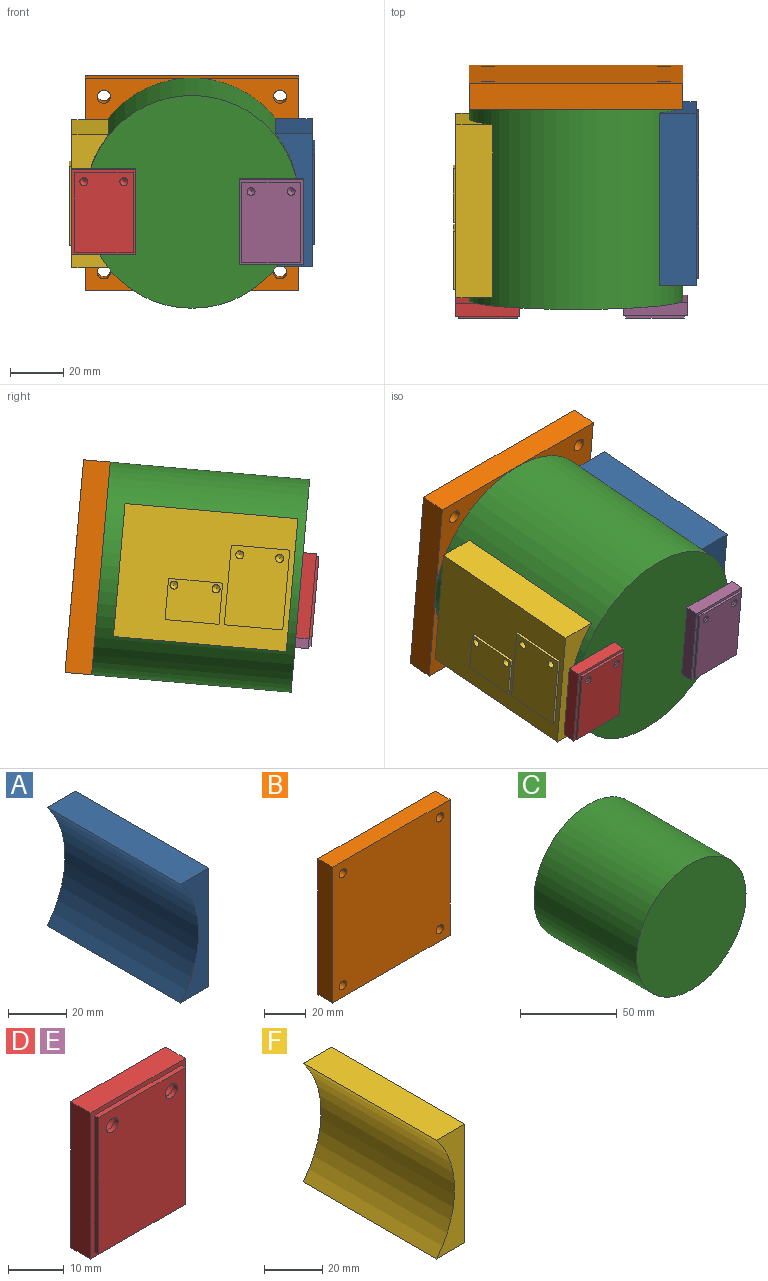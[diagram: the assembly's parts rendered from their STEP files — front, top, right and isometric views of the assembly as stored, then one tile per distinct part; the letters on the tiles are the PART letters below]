
ASSEMBLY  parts=6 mates=5
PART A: 35 faces, bbox 14.8x65x50 mm
  f0: plane 65x50mm, normal (1,0,0), area 1512mm2, adj f2,f3,f4,f5,f6,f7,f8,f9
  f1: cylinder r=40mm len=65mm, axis (0,1,0), area 3510.7mm2, adj f2,f3,f4,f5
  f2: plane 65x13.78mm, normal (0,0,-1), area 895.4mm2, adj f0,f1,f4,f5
  f3: plane 65x13.78mm, normal (0,0,1), area 895.4mm2, adj f0,f1,f4,f5
  f4: plane 50x13.78mm, normal (0,-1,0), area 389.2mm2, adj f0,f1,f2,f3
  f5: plane 50x13.78mm, normal (0,1,0), area 389.2mm2, adj f0,f1,f2,f3
  f6: plane 19x1mm, normal (0,0,1), area 19mm2, adj f0,f7,f9,f10
  f7: plane 34x1mm, normal (0,-1,0), area 34mm2, adj f0,f6,f8,f10
  f8: plane 19x1mm, normal (0,0,-1), area 19mm2, adj f0,f7,f9,f10
  f9: plane 34x1mm, normal (0,1,0), area 34mm2, adj f0,f6,f8,f10
  f10: plane 34x19mm, normal (1,0,0), area 636.2mm2, adj f6,f7,f8,f9,f26,f28
  f11: plane 16x1mm, normal (0,0,1), area 16mm2, adj f0,f12,f14,f15
  f12: plane 27x1mm, normal (0,-1,0), area 27mm2, adj f0,f11,f13,f15
  f13: plane 16x1mm, normal (0,0,-1), area 16mm2, adj f0,f12,f14,f15
  f14: plane 27x1mm, normal (0,1,0), area 27mm2, adj f0,f11,f13,f15
  f15: plane 27x16mm, normal (1,0,0), area 422.2mm2, adj f11,f12,f13,f14,f22,f24
  f16: plane 22x1mm, normal (0,0,1), area 22mm2, adj f0,f17,f19,f20
  f17: plane 30x1mm, normal (0,-1,0), area 30mm2, adj f0,f16,f18,f20
  f18: plane 22x1mm, normal (0,0,-1), area 22mm2, adj f0,f17,f19,f20
  f19: plane 30x1mm, normal (0,1,0), area 30mm2, adj f0,f16,f18,f20
  f20: plane 30x22mm, normal (1,0,0), area 626.2mm2, adj f16,f17,f18,f19,f30,f32,f34
  f21: cone r=0mm half-angle=59deg, axis (1,0,0), area 5.7mm2, adj f22
  f22: cylinder r=1.25mm len=5mm, axis (1,0,0), area 39.3mm2, adj f15,f21
  f23: cone r=0mm half-angle=59deg, axis (1,0,0), area 5.7mm2, adj f24
  f24: cylinder r=1.25mm len=5mm, axis (1,0,0), area 39.3mm2, adj f15,f23
  f25: cone r=0mm half-angle=59deg, axis (1,0,0), area 5.7mm2, adj f26
  f26: cylinder r=1.25mm len=5mm, axis (1,0,0), area 39.3mm2, adj f10,f25
  f27: cone r=0mm half-angle=59deg, axis (1,0,0), area 5.7mm2, adj f28
  f28: cylinder r=1.25mm len=5mm, axis (1,0,0), area 39.3mm2, adj f10,f27
  f29: cone r=0mm half-angle=59deg, axis (1,0,0), area 8.2mm2, adj f30
  f30: cylinder r=1.5mm len=5mm, axis (1,0,0), area 47.1mm2, adj f20,f29
  f31: cone r=0mm half-angle=59deg, axis (1,0,0), area 8.2mm2, adj f32
  f32: cylinder r=1.5mm len=5mm, axis (1,0,0), area 47.1mm2, adj f20,f31
  f33: cone r=0mm half-angle=59deg, axis (1,0,0), area 22.9mm2, adj f34
  f34: cylinder r=2.5mm len=5mm, axis (1,0,0), area 78.5mm2, adj f20,f33
PART B: 10 faces, bbox 80x10x80 mm
  f0: plane 80x10mm, normal (1,0,0), area 800mm2, adj f1,f6,f8,f9
  f1: plane 80x10mm, normal (0,0,1), area 800mm2, adj f0,f2,f8,f9
  f2: plane 80x10mm, normal (-1,0,0), area 800mm2, adj f1,f6,f8,f9
  f3: cylinder r=2.5mm len=10mm, axis (0,1,0), area 157.1mm2, adj f8,f9
  f4: cylinder r=2.5mm len=10mm, axis (0,1,0), area 157.1mm2, adj f8,f9
  f5: cylinder r=2.5mm len=10mm, axis (0,1,0), area 157.1mm2, adj f8,f9
  f6: plane 80x10mm, normal (0,0,-1), area 800mm2, adj f0,f2,f8,f9
  f7: cylinder r=2.5mm len=10mm, axis (0,1,0), area 157.1mm2, adj f8,f9
  f8: plane 80x80mm, normal (0,-1,0), area 6321.5mm2, adj f0,f1,f2,f3,f4,f5,f6,f7
  f9: plane 80x80mm, normal (0,1,0), area 6321.5mm2, adj f0,f1,f2,f3,f4,f5,f6,f7
PART C: 3 faces, bbox 80x75x80 mm
  f0: cylinder r=40mm len=80mm, axis (0,1,0), area 18849.6mm2, adj f1,f2
  f1: plane 80x80mm, normal (0,-1,0), area 5026.5mm2, adj f0
  f2: plane 80x80mm, normal (0,1,0), area 5026.5mm2, adj f0
PART D: 15 faces, bbox 24x6x32 mm
  f0: plane 22x1mm, normal (0,0,1), area 22mm2, adj f1,f3,f4,f9
  f1: plane 30x1mm, normal (-1,0,0), area 30mm2, adj f0,f2,f4,f9
  f2: plane 22x1mm, normal (0,0,-1), area 22mm2, adj f1,f3,f4,f9
  f3: plane 30x1mm, normal (1,0,0), area 30mm2, adj f0,f2,f4,f9
  f4: plane 30x22mm, normal (0,-1,0), area 645.9mm2, adj f0,f1,f2,f3,f12,f14
  f5: plane 32x5mm, normal (1,0,0), area 160mm2, adj f6,f8,f9,f10
  f6: plane 24x5mm, normal (0,0,1), area 120mm2, adj f5,f7,f9,f10
  f7: plane 32x5mm, normal (-1,0,0), area 160mm2, adj f6,f8,f9,f10
  f8: plane 24x5mm, normal (0,0,-1), area 120mm2, adj f5,f7,f9,f10
  f9: plane 32x24mm, normal (0,-1,0), area 108mm2, adj f0,f1,f2,f3,f5,f6,f7,f8
  f10: plane 32x24mm, normal (0,1,0), area 768mm2, adj f5,f6,f7,f8
  f11: cone r=0mm half-angle=59deg, axis (0,-1,0), area 8.2mm2, adj f12
  f12: cylinder r=1.5mm len=3mm, axis (0,-1,0), area 9.4mm2, adj f4,f11
  f13: cone r=0mm half-angle=59deg, axis (0,-1,0), area 8.2mm2, adj f14
  f14: cylinder r=1.5mm len=3mm, axis (0,-1,0), area 9.4mm2, adj f4,f13
PART E: same geometry as D
PART F: 24 faces, bbox 14.8x65x50 mm
  f0: plane 65x50mm, normal (1,0,0), area 2275.3mm2, adj f2,f3,f4,f5,f6,f7,f8,f9
  f1: cylinder r=40mm len=65mm, axis (0,1,0), area 3510.7mm2, adj f2,f3,f4,f5
  f2: plane 65x13.78mm, normal (0,0,-1), area 895.4mm2, adj f0,f1,f4,f5
  f3: plane 65x13.78mm, normal (0,0,1), area 895.4mm2, adj f0,f1,f4,f5
  f4: plane 50x13.78mm, normal (0,-1,0), area 389.2mm2, adj f0,f1,f2,f3
  f5: plane 50x13.78mm, normal (0,1,0), area 389.2mm2, adj f0,f1,f2,f3
  f6: plane 22x1mm, normal (0,0,1), area 22mm2, adj f0,f7,f9,f10
  f7: plane 30x1mm, normal (0,-1,0), area 30mm2, adj f0,f6,f8,f10
  f8: plane 22x1mm, normal (0,0,-1), area 22mm2, adj f0,f7,f9,f10
  f9: plane 30x1mm, normal (0,1,0), area 30mm2, adj f0,f6,f8,f10
  f10: plane 30x22mm, normal (1,0,0), area 645.9mm2, adj f6,f7,f8,f9,f21,f23
  f11: plane 15.5x1mm, normal (0,-1,0), area 15.5mm2, adj f0,f12,f14,f15
  f12: plane 20.3x1mm, normal (0,0,-1), area 20.3mm2, adj f0,f11,f13,f15
  f13: plane 15.5x1mm, normal (0,1,0), area 15.5mm2, adj f0,f12,f14,f15
  f14: plane 20.3x1mm, normal (0,0,1), area 20.3mm2, adj f0,f11,f13,f15
  f15: plane 20.3x15.5mm, normal (1,0,0), area 300.5mm2, adj f11,f12,f13,f14,f17,f19
  f16: cone r=0mm half-angle=59deg, axis (1,0,0), area 8.2mm2, adj f17
  f17: cylinder r=1.5mm len=5mm, axis (1,0,0), area 47.1mm2, adj f15,f16
  f18: cone r=0mm half-angle=59deg, axis (1,0,0), area 8.2mm2, adj f19
  f19: cylinder r=1.5mm len=5mm, axis (1,0,0), area 47.1mm2, adj f15,f18
  f20: cone r=0mm half-angle=59deg, axis (1,0,0), area 8.2mm2, adj f21
  f21: cylinder r=1.5mm len=5mm, axis (1,0,0), area 47.1mm2, adj f10,f20
  f22: cone r=0mm half-angle=59deg, axis (1,0,0), area 8.2mm2, adj f23
  f23: cylinder r=1.5mm len=5mm, axis (1,0,0), area 47.1mm2, adj f10,f22
PLACE A rot(axis=(1,0,0),5deg) t=(-86.9,74.34,-13.03)mm
PLACE B rot(axis=(1,0,0),5deg) t=(-86.9,86.74,-11.95)mm
PLACE C rot(axis=(1,0,0),5deg) t=(-86.9,76.78,-12.82)mm
PLACE D rot(axis=(1,0,0),5deg) t=(-119.94,2.37,-22.86)mm
PLACE E rot(axis=(1,0,0),5deg) t=(-57.29,2.69,-26.5)mm
PLACE F rot(axis=(0,0.04,-1),180deg) t=(-86.9,5.16,-19.08)mm
MATE planar D.f10 <-> C.f0  axis (0,1,0.09) through (-119.94,0.98,-6.92)mm
MATE slider F.f1 <-> C.f0  axis (0,-1,-0.09) through (-86.9,37.54,-16.25)mm
MATE fastened C.f0 <-> B.f8  axis (0,1,0.09) through (-86.9,76.78,-12.82)mm
MATE cylindrical A.f1 <-> C.f0  axis (0,1,0.09) through (-86.9,41.97,-15.86)mm
MATE planar E.f10 <-> C.f0  axis (0,1,0.09) through (-57.29,2.69,-26.5)mm
